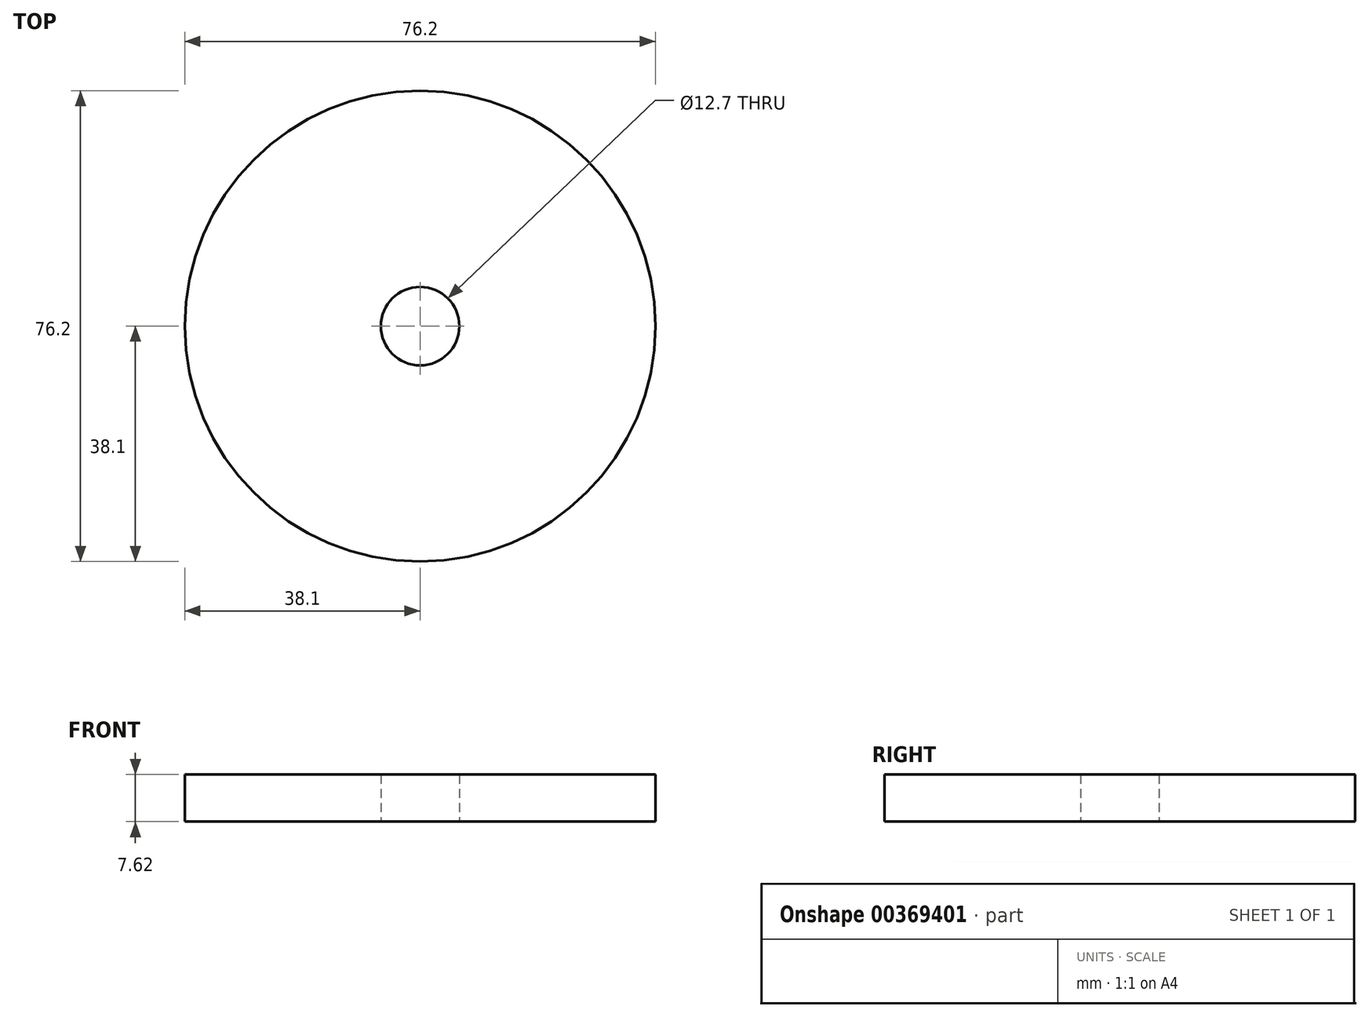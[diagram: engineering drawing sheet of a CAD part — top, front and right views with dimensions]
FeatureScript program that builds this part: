
annotation { "Feature Type Name" : "Feature", "Feature Type Description" : "" }
export const myFeature = defineFeature(function(context is Context, id is Id, definition is map)
    precondition{}
    {
        {
            var Q0;
            Q0=qCreatedBy(makeId("Top.planeOp"),FACE);
            var sketch = newSketch(context, id + "F0", { "sketchPlane" : qUnion([Q0])});
            skCircle(sketch, "E0", {"center": v(0, 0) * mm, "radius": 38.1 * mm});
            skCircle(sketch, "E1", {"center": v(0, 0) * mm, "radius": 6.35 * mm});
            skSolve(sketch);
        }
        {
            var Q0;
            Q0=qSketchRegion(id+"F0",true);
            extrude(context, id + "F1", {"entities" : qUnion([Q0]), "depth" : 7.62 * mm});
        }
    });
